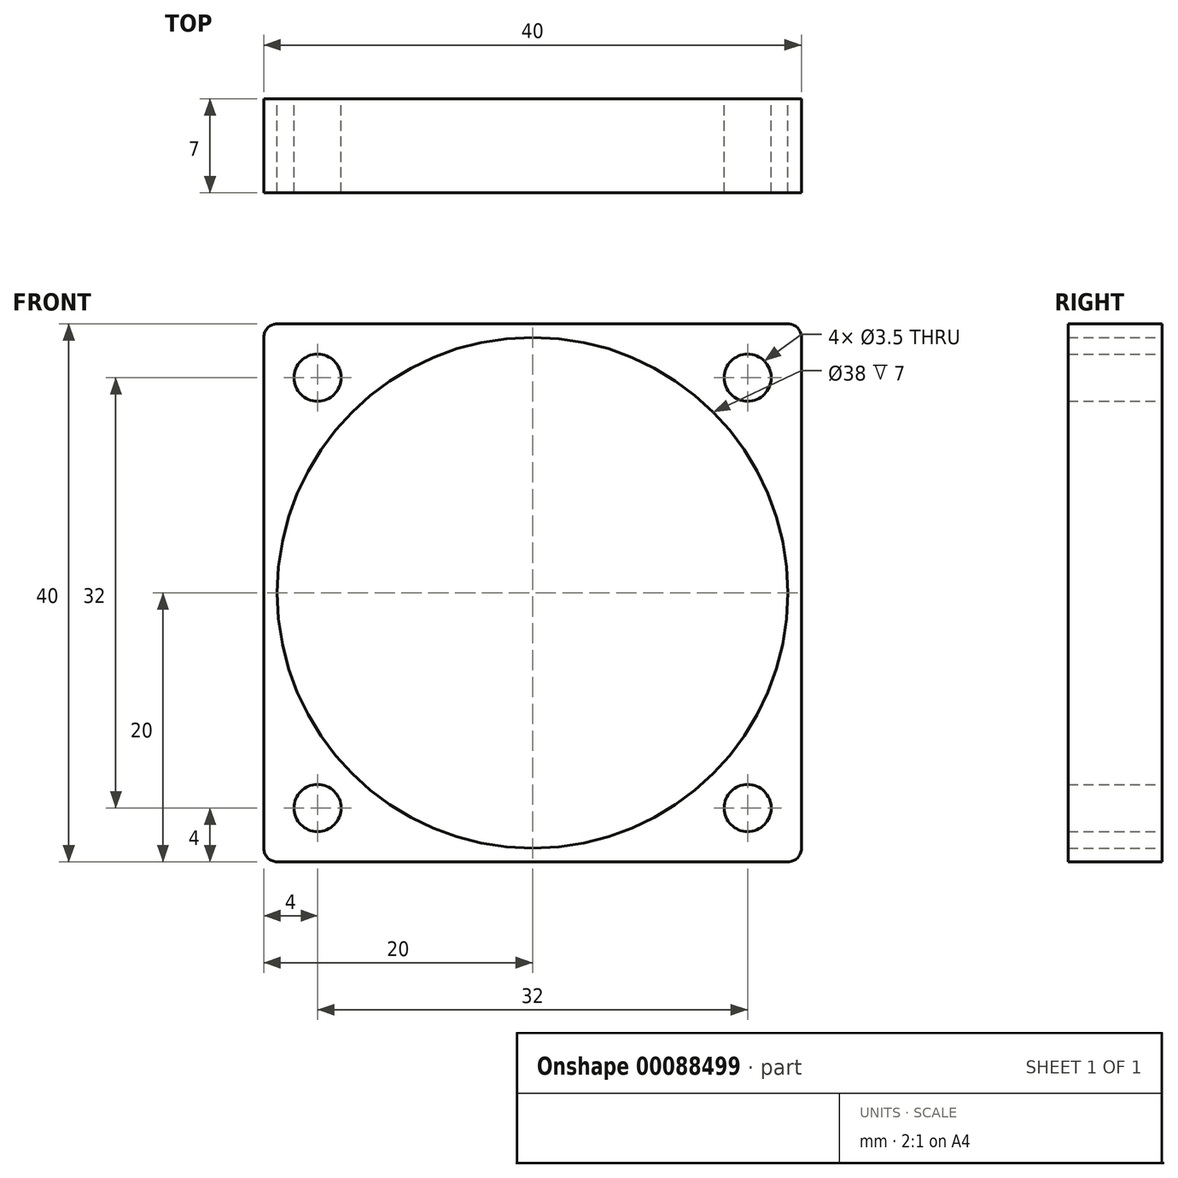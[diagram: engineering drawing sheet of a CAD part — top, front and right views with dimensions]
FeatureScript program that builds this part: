
annotation { "Feature Type Name" : "Feature", "Feature Type Description" : "" }
export const myFeature = defineFeature(function(context is Context, id is Id, definition is map)
    precondition{}
    {
        {
            var Q0;
            Q0=qCreatedBy(makeId("Front.planeOp"),FACE);
            var sketch = newSketch(context, id + "F0", { "sketchPlane" : qUnion([Q0])});
            skLineSegment(sketch, "E0.bottom", {"start": v(-20, 20) * mm, "end": v(20, 20) * mm});
            skLineSegment(sketch, "E0.top", {"start": v(-20, -20) * mm, "end": v(20, -20) * mm});
            skLineSegment(sketch, "E0.left", {"start": v(-20, 20) * mm, "end": v(-20, -20) * mm});
            skLineSegment(sketch, "E0.right", {"start": v(20, 20) * mm, "end": v(20, -20) * mm});
            skLineSegment(sketch, "E1", {"start": v(-20, 20) * mm, "end": v(20, -20) * mm, "construction": true});
            skCircle(sketch, "E2", {"center": v(-16, 16) * mm, "radius": 1.75 * mm});
            skLineSegment(sketch, "E3.bottom", {"start": v(-16, 16) * mm, "end": v(16, 16) * mm, "construction": true});
            skLineSegment(sketch, "E3.top", {"start": v(-16, -16) * mm, "end": v(16, -16) * mm, "construction": true});
            skLineSegment(sketch, "E3.left", {"start": v(-16, 16) * mm, "end": v(-16, -16) * mm, "construction": true});
            skLineSegment(sketch, "E3.right", {"start": v(16, 16) * mm, "end": v(16, -16) * mm, "construction": true});
            skLineSegment(sketch, "E4", {"start": v(-16, -16) * mm, "end": v(0, 0) * mm, "construction": true});
            skCircle(sketch, "E5", {"center": v(16, 16) * mm, "radius": 1.75 * mm});
            skCircle(sketch, "E6", {"center": v(16, -16) * mm, "radius": 1.75 * mm});
            skCircle(sketch, "E7", {"center": v(-16, -16) * mm, "radius": 1.75 * mm});
            skCircle(sketch, "E8", {"center": v(0, 0) * mm, "radius": 19 * mm});
            skSolve(sketch);
        }
        {
            var Q0;
            Q0=makeQuery(id+"F0.imprint","IMPRINT",FACE,{"disambiguationData":[TD([[makeQuery(id+"F0.imprint","IMPRINT",EDGE,{"derivedFrom":sQuery(id+"F0.wireOp",EDGE,"E0.bottom")}),-1.0]])]});
            extrude(context, id + "F1", {"entities" : qUnion([Q0]), "depth" : 7 * mm});
        }
        {
            var Q0;
            Q0=makeQuery(id+"F1.opExtrude","SWEPT_EDGE",EDGE,{"disambiguationData":[OSD([sQuery(id+"F0.wireOp",EDGE,"E0.top"),sQuery(id+"F0.wireOp",EDGE,"E0.right")])]});
            var Q1;
            Q1=makeQuery(id+"F1.opExtrude","SWEPT_EDGE",EDGE,{"disambiguationData":[OSD([sQuery(id+"F0.wireOp",EDGE,"E0.top"),sQuery(id+"F0.wireOp",EDGE,"E0.left")])]});
            var Q2;
            Q2=makeQuery(id+"F1.opExtrude","SWEPT_EDGE",EDGE,{"disambiguationData":[OSD([sQuery(id+"F0.wireOp",EDGE,"E0.bottom"),sQuery(id+"F0.wireOp",EDGE,"E0.right")])]});
            var Q3;
            Q3=makeQuery(id+"F1.opExtrude","SWEPT_EDGE",EDGE,{"disambiguationData":[OSD([sQuery(id+"F0.wireOp",EDGE,"E0.bottom"),sQuery(id+"F0.wireOp",EDGE,"E0.left")])]});
            fillet(context, id + "F2", {"entities" : qUnion([Q0, Q1, Q2, Q3]), "radius" : 1 * mm, "tangentPropagation" : true, "allowEdgeOverflow" : false});
        }
    });
